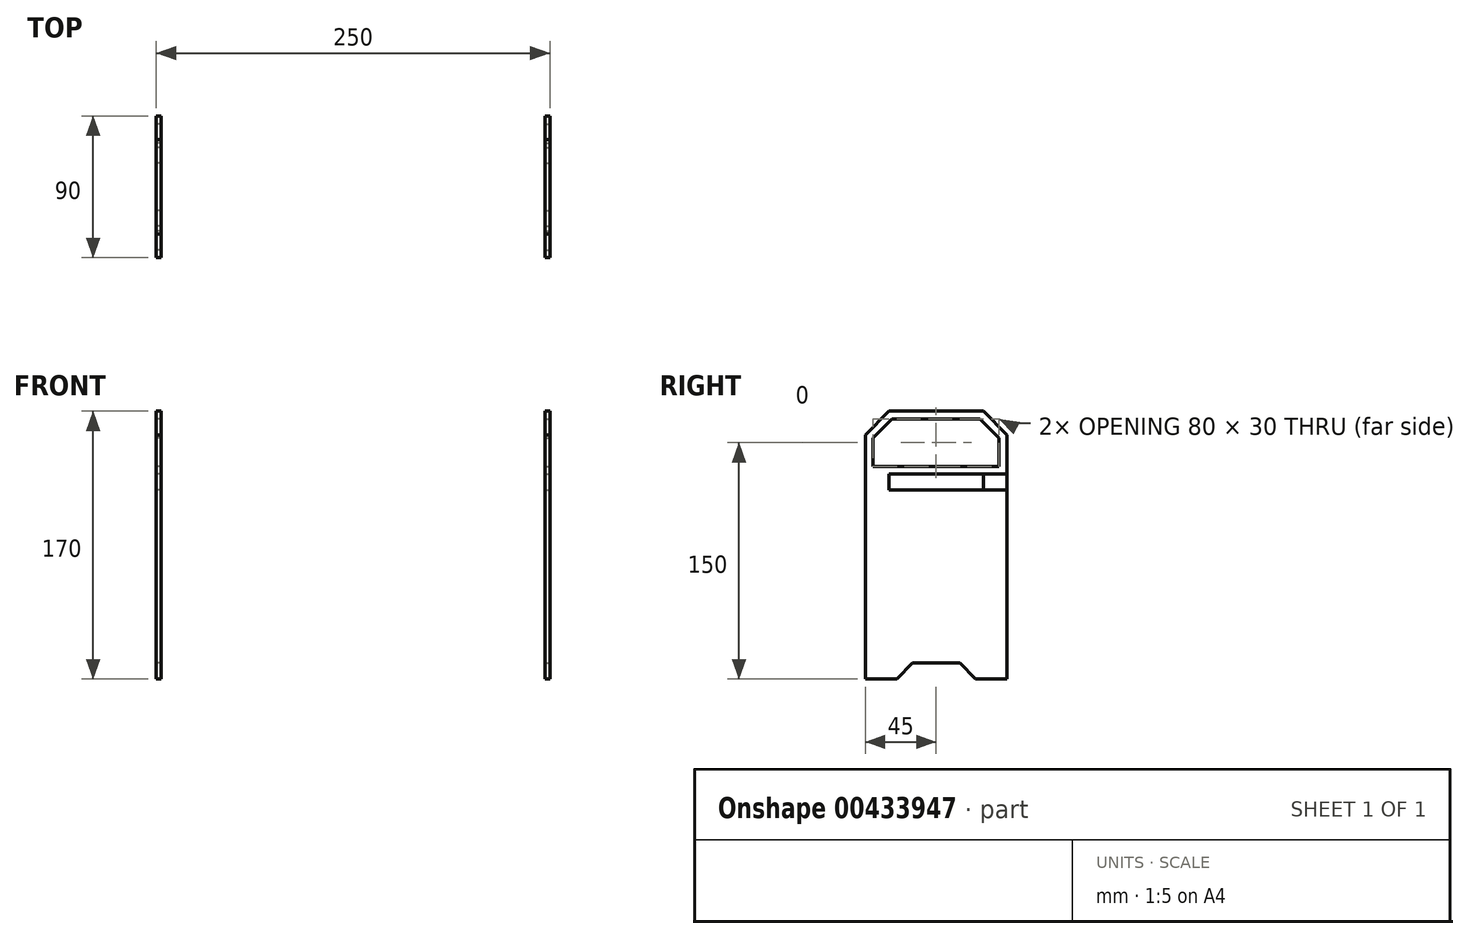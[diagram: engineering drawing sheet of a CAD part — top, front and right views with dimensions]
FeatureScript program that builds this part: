
annotation { "Feature Type Name" : "Feature", "Feature Type Description" : "" }
export const myFeature = defineFeature(function(context is Context, id is Id, definition is map)
    precondition{}
    {
        {
            var Q0;
            Q0=qCreatedBy(makeId("Top.planeOp"),FACE);
            var sketch = newSketch(context, id + "F0", { "sketchPlane" : qUnion([Q0])});
            skLineSegment(sketch, "E0.bottom", {"start": v(-125, -45) * mm, "end": v(125, -45) * mm});
            skLineSegment(sketch, "E0.top", {"start": v(-125, 45) * mm, "end": v(125, 45) * mm});
            skLineSegment(sketch, "E0.left", {"start": v(-125, -45) * mm, "end": v(-125, 45) * mm});
            skLineSegment(sketch, "E0.right", {"start": v(125, -45) * mm, "end": v(125, 45) * mm});
            skPoint(sketch, "E0.middle", {"position": v(0, 0) * mm});
            skLineSegment(sketch, "E1.bottom", {"start": v(-125, 45) * mm, "end": v(-122, 45) * mm});
            skLineSegment(sketch, "E1.top", {"start": v(-125, 30) * mm, "end": v(-122, 30) * mm});
            skLineSegment(sketch, "E1.left", {"start": v(-125, 45) * mm, "end": v(-125, 30) * mm});
            skLineSegment(sketch, "E1.right", {"start": v(-122, 45) * mm, "end": v(-122, 30) * mm});
            skLineSegment(sketch, "E2.MirrorCS", {"start": v(125, 45) * mm, "end": v(122, 45) * mm});
            skLineSegment(sketch, "E3.MirrorCS", {"start": v(125, 30) * mm, "end": v(122, 30) * mm});
            skLineSegment(sketch, "E4.MirrorCS", {"start": v(125, 45) * mm, "end": v(125, 30) * mm});
            skLineSegment(sketch, "E5.MirrorCS", {"start": v(122, 45) * mm, "end": v(122, 30) * mm});
            skLineSegment(sketch, "E6.MirrorCS", {"start": v(125, -45) * mm, "end": v(122, -45) * mm});
            skLineSegment(sketch, "E7.MirrorCS", {"start": v(-125, -45) * mm, "end": v(-122, -45) * mm});
            skLineSegment(sketch, "E8.MirrorCS", {"start": v(-125, -30) * mm, "end": v(-122, -30) * mm});
            skLineSegment(sketch, "E9.MirrorCS", {"start": v(125, -30) * mm, "end": v(122, -30) * mm});
            skLineSegment(sketch, "E10.MirrorCS", {"start": v(-125, -45) * mm, "end": v(-125, -30) * mm});
            skLineSegment(sketch, "E11.MirrorCS", {"start": v(-122, -45) * mm, "end": v(-122, -30) * mm});
            skLineSegment(sketch, "E12.MirrorCS", {"start": v(125, -45) * mm, "end": v(125, -30) * mm});
            skLineSegment(sketch, "E13.MirrorCS", {"start": v(122, -45) * mm, "end": v(122, -30) * mm});
            skSolve(sketch);
        }
        {
            var Q0;
            Q0=makeQuery(id+"F0.imprint","IMPRINT",FACE,{"disambiguationData":[TD([[makeQuery(id+"F0.imprint","IMPRINT",EDGE,{"derivedFrom":sQuery(id+"F0.wireOp",EDGE,"E0.top")}),-1.0]])]});
            extrude(context, id + "F1", {"entities" : qUnion([Q0]), "depth" : 10 * mm});
        }
        {
            var Q0;
            Q0=makeQuery(id+"F1.opExtrude","SWEPT_FACE",FACE,{"disambiguationData":[OSD([sQuery(id+"F0.wireOp",EDGE,"E0.left")])]});
            var sketch = newSketch(context, id + "F2", { "sketchPlane" : qUnion([Q0])});
            skLineSegment(sketch, "E14.top", {"start": v(30, 50) * mm, "end": v(-30, 50) * mm});
            skLineSegment(sketch, "E14.left", {"start": v(45, -50) * mm, "end": v(45, 35) * mm});
            skLineSegment(sketch, "E14.right", {"start": v(-45, -50) * mm, "end": v(-45, 35) * mm});
            skPoint(sketch, "E14.middle", {"position": v(0, 0) * mm});
            skLineSegment(sketch, "E15.bottom", {"start": v(-30, 0) * mm, "end": v(30, 0) * mm});
            skLineSegment(sketch, "E15.top", {"start": v(-30, 10) * mm, "end": v(30, 10) * mm});
            skLineSegment(sketch, "E15.left", {"start": v(-30, 0) * mm, "end": v(-30, 10) * mm});
            skLineSegment(sketch, "E15.right", {"start": v(30, 0) * mm, "end": v(30, 10) * mm});
            skLineSegment(sketch, "E16.left", {"start": v(-45, -50) * mm, "end": v(-45, -120) * mm});
            skLineSegment(sketch, "E16.right", {"start": v(45, -50) * mm, "end": v(45, -120) * mm});
            skLineSegment(sketch, "E17", {"start": v(-45, -120) * mm, "end": v(-25, -120) * mm});
            skLineSegment(sketch, "E18", {"start": v(45, -120) * mm, "end": v(25, -120) * mm});
            skLineSegment(sketch, "E19", {"start": v(25, -120) * mm, "end": v(15, -110) * mm});
            skLineSegment(sketch, "E20.MirrorCS", {"start": v(-25, -120) * mm, "end": v(-15, -110) * mm});
            skLineSegment(sketch, "E21", {"start": v(-15, -110) * mm, "end": v(15, -110) * mm});
            skLineSegment(sketch, "E22", {"start": v(30, 50) * mm, "end": v(45, 35) * mm});
            skLineSegment(sketch, "E23.MirrorCS", {"start": v(-30, 50) * mm, "end": v(-45, 35) * mm});
            skLineSegment(sketch, "E24", {"start": v(-40, 15) * mm, "end": v(-40, 32.93) * mm});
            skLineSegment(sketch, "E25", {"start": v(-40, 32.93) * mm, "end": v(-27.93, 45) * mm});
            skLineSegment(sketch, "E26.MirrorCS", {"start": v(40, 32.93) * mm, "end": v(27.93, 45) * mm});
            skLineSegment(sketch, "E27.MirrorCS", {"start": v(40, 15) * mm, "end": v(40, 32.93) * mm});
            skLineSegment(sketch, "E28", {"start": v(-40, 15) * mm, "end": v(40, 15) * mm});
            skLineSegment(sketch, "E29", {"start": v(-27.93, 45) * mm, "end": v(27.93, 45) * mm});
            skSolve(sketch);
        }
        {
            var Q0;
            Q0=makeQuery(id+"F2.imprint","IMPRINT",FACE,{"disambiguationData":[TD([[makeQuery(id+"F2.imprint","IMPRINT",EDGE,{"derivedFrom":sQuery(id+"F2.wireOp",EDGE,"E14.top")}),1.0]])]});
            extrude(context, id + "F3", {"entities" : qUnion([Q0]), "oppositeDirection" : true, "depth" : 3 * mm});
        }
        {
            var Q0;
            Q0=makeQuery(id+"F3.opExtrude","SWEPT_BODY",BODY,{"disambiguationData":[OSD([sQuery(id+"F2.wireOp",EDGE,"E14.top"),sQuery(id+"F2.wireOp",EDGE,"E14.left"),sQuery(id+"F2.wireOp",EDGE,"E14.right"),sQuery(id+"F2.wireOp",EDGE,"E15.bottom"),sQuery(id+"F2.wireOp",EDGE,"E15.top"),sQuery(id+"F2.wireOp",EDGE,"E15.left"),sQuery(id+"F2.wireOp",EDGE,"E15.right"),sQuery(id+"F2.wireOp",EDGE,"E16.left"),sQuery(id+"F2.wireOp",EDGE,"E16.right"),sQuery(id+"F2.wireOp",EDGE,"E17"),sQuery(id+"F2.wireOp",EDGE,"E18"),sQuery(id+"F2.wireOp",EDGE,"E19"),sQuery(id+"F2.wireOp",EDGE,"E20.MirrorCS"),sQuery(id+"F2.wireOp",EDGE,"E21"),sQuery(id+"F2.wireOp",EDGE,"E22"),sQuery(id+"F2.wireOp",EDGE,"E23.MirrorCS"),sQuery(id+"F2.wireOp",EDGE,"E24"),sQuery(id+"F2.wireOp",EDGE,"E25"),sQuery(id+"F2.wireOp",EDGE,"E26.MirrorCS"),sQuery(id+"F2.wireOp",EDGE,"E27.MirrorCS"),sQuery(id+"F2.wireOp",EDGE,"E28"),sQuery(id+"F2.wireOp",EDGE,"E29")])]});
            var Q1;
            Q1=qCreatedBy(makeId("Right.planeOp"),FACE);
            mirror(context, id + "F4", {"entities" : qUnion([Q0]), "mirrorPlane" : qUnion([Q1])});
        }
    });
